# Revit family: Metal_Vented_Lockers-Salsbury_Industries-71000_Series-3_Wide_Units
name_source: partatom
category: Specialty Equipment
revit_build: Autodesk Revit 2016 (Build: 20150714_1515(x64)
units: mm (PartAtom-declared; Revit-internal decimal feet)

## family parameters
Always vertical = Yes
Cut with Voids When Loaded = No
OmniClass Number = 23.40.00.00
OmniClass Title = Equipment and Furnishings
Part Type = Normal
Room Calculation Point = No
Round Connector Dimension = Use Diameter
Shared = No
Work Plane-Based = No

## types (18) — shared parameters
Assembly Code = C1030310
Manufacturer = Salsbury Industries
MasterFormat Number = 10 51 13
MasterFormat Title = Lockers
OmniClass 23 Number = 23.40.00.00
Type Comments = 12" Wide Vented Metal Locker - Single Tier
URL = www.lockers.com
Vent Array Spacing = 1.187 "
Version = 2.0 (01/30/18)
Width = 36.04 "

## per-type parameters (varying)
| type | Base Height | Depth | Description | Door Location D1 | Hasp Handle Material | Hasp Plate Rivet Material | Model | OmniClass 23 Title | Sloping Hood Height | Standard Leg Base | Unit Height | Vent Array 1 | Vent Array 2 | Vent Configuration Height | Vent Offset | Zee Base |
| 71362 - with Standard 6" High Legs | 6 " | 12.01 " | 3 Wide - 6 Feet High - 12 Inches Deep | Vented Metal Locker Doors-12 inch with Hasps : Single Tier Door - 6 foot | Plastic - Salsbury Finish = Black | Steel -Salsbury Finish =  Polished Steel | 71362 | Equipment and Furnishings | 6.625 " | Metal Locker Legs - 3 Wide : 6" High - 36" W x 12" D | 72 " | 6 | 5 | Vents : 6 foot high vents | 3.25 " | Metal Locker Zee Base - 3 Wide : None |
| 71365 - with Standard 6" High Legs | 6 " | 15.01 " | 3 Wide - 6 Feet High - 15 Inches Deep | Vented Metal Locker Doors-12 inch with Hasps : Single Tier Door - 6 foot | Plastic - Salsbury Finish - Black | Steel -Salsbury Finish - Polished Steel | 71365 | Equipment and Furnishings | 8.682 " | Metal Locker Legs - 3 Wide : 6" High - 36" W x 15" D | 72 " | 8 | 7 | Vents : 6 foot high vents | 3.5 " | Metal Locker Zee Base - 3 Wide : None |
| 71368 - with Standard 6" High Legs | 6 " | 18.01 " | 3 Wide - 6 Feet High - 18 Inches Deep | Vented Metal Locker Doors-12 inch with Hasps : Single Tier Door - 6 foot | Plastic - Salsbury Finish - Black | Steel -Salsbury Finish - Polished Steel | 71368 | Equipment and Furnishings | 10.739 " | Metal Locker Legs - 3 Wide : 6" High - 36"W x 18"D | 72 " | 10 | 9 | Vents : 6 foot high vents | 3.75 " | Metal Locker Zee Base - 3 Wide : None |
| 71362 - with 77572 Zee Base and 77550 Lockers without Legs | 4 " | 12.01 " | 3 Wide - 6 Feet High - 12 Inches Deep with Zee Base and Lockers without Legs | Vented Metal Locker Doors-12 inch with Hasps : Single Tier Door - 6 foot | Plastic - Salsbury Finish - Black | Steel -Salsbury Finish - Polished Steel | 71362 with 77572 and 77550 | Equipment and Furnishings | 6.625 " | Metal Locker Legs - 3 Wide : No Legs | 72 " | 6 | 5 | Vents : 6 foot high vents | 3.25 " | Metal Locker Zee Base - 3 Wide : 77572- 36" W x 12" D |
| 71365 - with 77575 Zee Base and 77550 Lockers without Legs | 4 " | 15.01 " | 3 Wide - 6 Feet High - 15 Inches Deep with Zee Base and Lockers without Legs | Vented Metal Locker Doors-12 inch with Hasps : Single Tier Door - 6 foot | Plastic - Salsbury Finish - Black | Steel -Salsbury Finish - Polished Steel | 71365 with 77575 and 77550 | Equipment and Furnishings | 8.682 " | Metal Locker Zee Base - 3 Wide : None | 72 " | 8 | 7 | Vents : 6 foot high vents | 3.5 " | Metal Locker Zee Base - 3 Wide : 77575 - 36" W x 15" D |
| 71368 - with 77578 Zee Base and 77550 Lockers without Legs | 4 " | 18.01 " | 3 Wide - 6 Feet High - 18 Inches Deep with Zee Base and Lockers without Legs | Vented Metal Locker Doors-12 inch with Hasps : Single Tier Door - 6 foot | Plastic - Salsbury Finish - Black | Steel -Salsbury Finish - Polished Steel | 71368 with 77578 and 77550 | Equipment aqnd Furnishings | 10.739 " | Metal Locker Zee Base - 3 Wide : None | 72 " | 10 | 9 | Vents : 6 foot high vents | 3.75 " | Metal Locker Zee Base - 3 Wide : 77578 - 36"W x 18"D |
| 71362 - with 77550 Lockers without Legs | 0 " | 12.01 " | 3 Wide - 6 Feet High - 12 Inches Deep with Lockers without Legs | Vented Metal Locker Doors-12 inch with Hasps : Single Tier Door - 6 foot | Plastic - Salsbury Finish - Black | Steel -Salsbury Finish - Polished Steel | 71362 with 77550 | Equipment and Furnishings | 6.625 " | Metal Locker Zee Base - 3 Wide : None | 72 " | 6 | 5 | Vents : 6 foot high vents | 3.25 " | Metal Locker Zee Base - 3 Wide : None |
| 71365 - with 77550 Lockers without Legs | 0 " | 15.01 " | 3 Wide - 6 Feet High - 15 Inches Deep with Lockers without Legs | Vented Metal Locker Doors-12 inch with Hasps : Single Tier Door - 6 foot | Plastic - Salsbury Finish - Black | Steel -Salsbury Finish - Polished Steel | 71365 with 77550 | Equipment and Furnishings | 8.682 " | Metal Locker Legs - 3 Wide : No Legs | 72 " | 8 | 7 | Vents : 6 foot high vents | 3.5 " | Metal Locker Zee Base - 3 Wide : None |
| 71368 - with 77550 Lockers without Legs | 0 " | 18.01 " | 3 Wide - 6 Feet High - 18 Inches Deep with Lockers without Legs | Vented Metal Locker Doors-12 inch with Hasps : Single Tier Door - 6 foot | Plastic - Salsbury Finish - Black | Steel -Salsbury Finish - Polished Steel | 71368 with 77550 | Equipment and Furnishings | 10.739 " | Metal Locker Legs - 3 Wide : No Legs | 72 " | 10 | 9 | Vents : 6 foot high vents | 3.75 " | Metal Locker Zee Base - 3 Wide : None |
| 71352 - with Standard 6" High Legs | 6 " | 12.01 " | 3 Wide - 5 Feet High - 12 Inches Deep | Vented Metal Locker Doors-12 inch with Hasps : Single Tier Door - 5 foot | Plastic - Salsbury Finish - Black | Steel -Salsbury Finish - Polished Steel | 71352 | Equipment and Furnishings | 6.625 " | Metal Locker Legs - 3 Wide : 6" High - 36" W x 12" D | 60 " | 6 | 5 | Vents : 5 foot high vents | 3.25 " | Metal Locker Zee Base - 3 Wide : None |
| 71352 - with 77572 Zee Base and 77550 Lockers without Legs | 4 " | 12.01 " | 3 Wide - 5 Feet High - 12 Inches Deep with Zee Base and Lockers without Legs | Vented Metal Locker Doors-12 inch with Hasps : Single Tier Door - 5 foot | Plastic - Salsbury Finish - Black | Steel -Salsbury Finish - Polished Steel | 71352 with 77572 and 77550 | Equipment and Furnishings | 6.625 " | Metal Locker Zee Base - 3 Wide : None | 60 " | 6 | 5 | Vents : 5 foot high vents | 3.25 " | Metal Locker Zee Base - 3 Wide : 77572- 36" W x 12" D |
| 71352 - with 77550 Lockers without Legs | 0 " | 12.01 " | 3 Wide - 5 Feet High - 12 Inches Deep with Lockers without Legs | Vented Metal Locker Doors-12 inch with Hasps : Single Tier Door - 5 foot | Plastic - Salsbury Finish - Black | Steel -Salsbury Finish - Polished Steel | 71352 with 77550 | Equipment and Furnishings | 6.625 " | Metal Locker Legs - 3 Wide : No Legs | 60 " | 6 | 5 | Vents : 5 foot high vents | 3.25 " | Metal Locker Zee Base - 3 Wide : None |
| 71355 - with Standard 6" High Legs | 6 " | 15.01 " | 3 Wide - 5 Feet High - 15 Inches Deep | Vented Metal Locker Doors-12 inch with Hasps : Single Tier Door - 5 foot | Plastic - Salsbury Finish - Black | Steel -Salsbury Finish - Polished Steel | 71355 | Equipment and Furnishings | 8.682 " | Metal Locker Legs - 3 Wide : 6" High - 36" W x 15" D | 60 " | 8 | 7 | Vents : 5 foot high vents | 3.5 " | Metal Locker Zee Base - 3 Wide : None |
| 71355 - with 77575 Zee Base and 77550 Lockers without Legs | 4 " | 15.01 " | 3 Wide - 5 Feet High - 15 Inches Deep with Zee Base and Lockers without Legs | Vented Metal Locker Doors-12 inch with Hasps : Single Tier Door - 5 foot | Plastic - Salsbury Finish - Black | Steel -Salsbury Finish - Polished Steel | 71355 with 77575 and 77550 | Equipment and Furnishings | 8.682 " | Metal Locker Zee Base - 3 Wide : None | 60 " | 8 | 7 | Vents : 5 foot high vents | 3.5 " | Metal Locker Zee Base - 3 Wide : 77575 - 36" W x 15" D |
| 71355 - with 77550 Lockers without Legs | 0 " | 15.01 " | 3 Wide - 5 Feet High - 15 Inches Deep with Lockers without Legs | Vented Metal Locker Doors-12 inch with Hasps : Single Tier Door - 5 foot | Plastic - Salsbury Finish - Black | Steel -Salsbury Finish - Polished Steel | 71355 with 77550 | Equipment and Furnishings | 8.682 " | Metal Locker Legs - 3 Wide : No Legs | 60 " | 8 | 7 | Vents : 5 foot high vents | 3.5 " | Metal Locker Zee Base - 3 Wide : None |
| 71358 - with Standard 6" High Legs | 6 " | 18.01 " | 3 Wide - 5 Feet High - 18 Inches Deep | Vented Metal Locker Doors-12 inch with Hasps : Single Tier Door - 5 foot | Plastic - Salsbury Finish - Black | Steel -Salsbury Finish - Polished Steel | 71358 | Equipment and Furnishings | 10.739 " | Metal Locker Legs - 3 Wide : 6" High - 36"W x 18"D | 60 " | 10 | 9 | Vents : 5 foot high vents | 3.75 " | Metal Locker Zee Base - 3 Wide : None |
| 71358 - with 77578 Zee Base and 77550 Lockers without Legs | 4 " | 18.01 " | 3 Wide - 5 Feet High - 18 Inches Deep with Zee Base and Lockers without Legs | Vented Metal Locker Doors-12 inch with Hasps : Single Tier Door - 5 foot | Plastic - Salsbury Finish - Black | Steel -Salsbury Finish - Polished Steel | 71358 with 77578 and 77550 | Equipment and Furnishings | 10.739 " | Metal Locker Zee Base - 3 Wide : None | 60 " | 10 | 9 | Vents : 5 foot high vents | 3.75 " | Metal Locker Zee Base - 3 Wide : 77578 - 36"W x 18"D |
| 71358 - with 77550 Lockers without Legs | 0 " | 18.01 " | 3 Wide - 5 Feet High - 18 Inches Deep with Lockers without Legs | Vented Metal Locker Doors-12 inch with Hasps : Single Tier Door - 5 foot | Plastic - Salsbury Finish - Black | Steel -Salsbury Finish - Polished Steel | 71358 with 77550 | Equipment and Furnishings | 10.739 " | Metal Locker Legs - 3 Wide : No Legs | 60 " | 10 | 9 | Vents : 5 foot high vents | 3.75 " | Metal Locker Zee Base - 3 Wide : None |

## geometry (parser evidence)
native form markers: Sweep x58
no freeform markers — native parametric forms only
